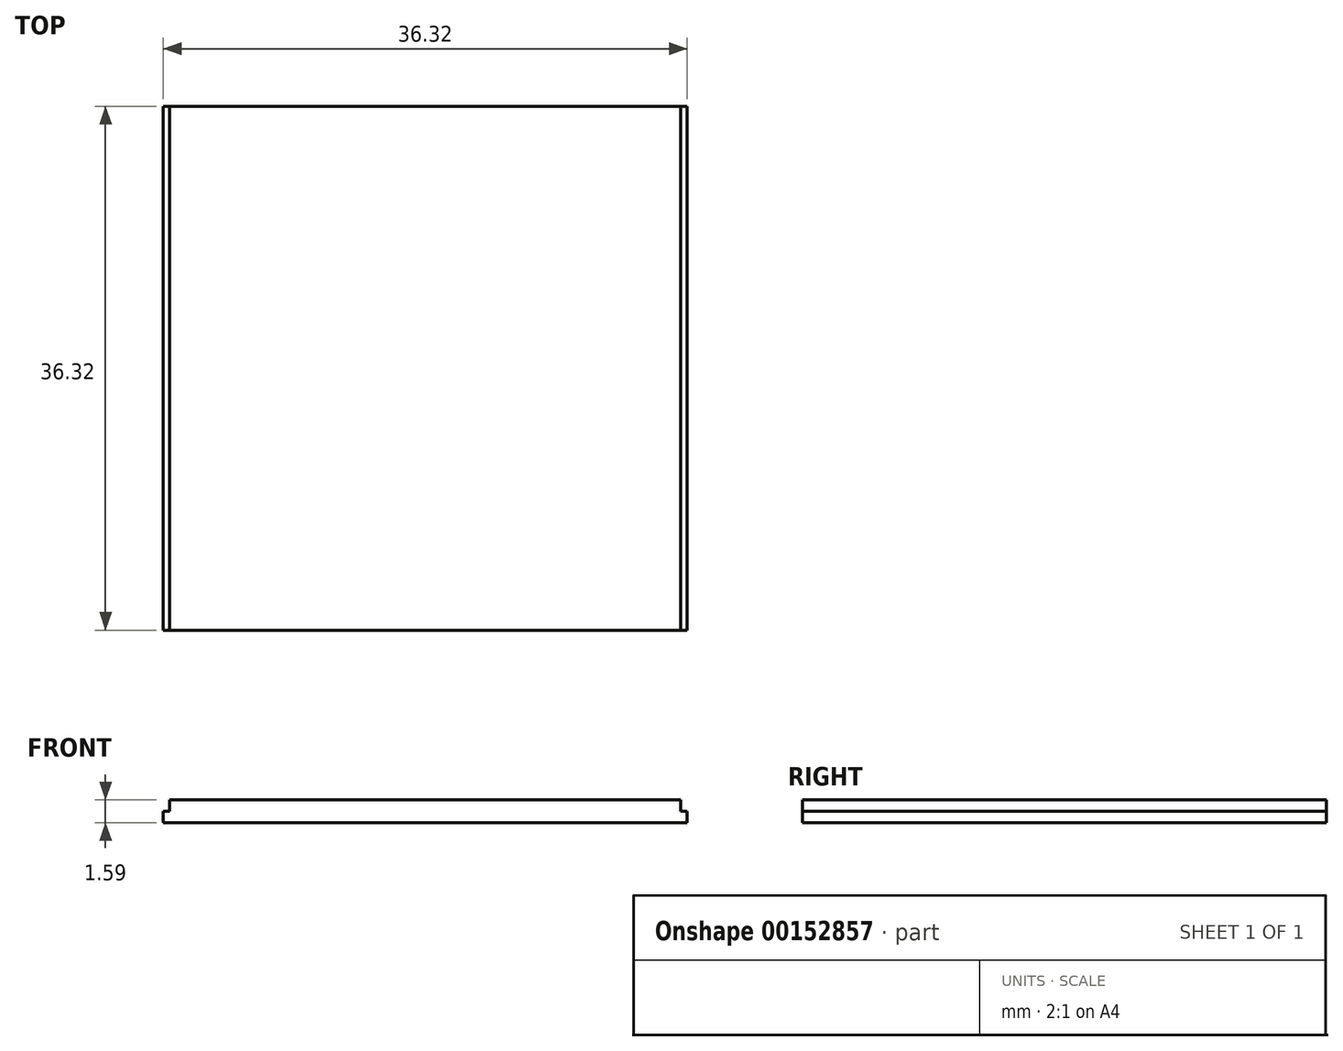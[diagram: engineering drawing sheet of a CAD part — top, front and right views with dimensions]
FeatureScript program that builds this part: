
annotation { "Feature Type Name" : "Feature", "Feature Type Description" : "" }
export const myFeature = defineFeature(function(context is Context, id is Id, definition is map)
    precondition{}
    {
        {
            var Q0;
            Q0=qCreatedBy(makeId("Top.planeOp"),FACE);
            var sketch = newSketch(context, id + "F0", { "sketchPlane" : qUnion([Q0])});
            skLineSegment(sketch, "E0.bottom", {"start": v(0, 0) * mm, "end": v(36.32, 0) * mm});
            skLineSegment(sketch, "E0.top", {"start": v(0, -36.32) * mm, "end": v(36.32, -36.32) * mm});
            skLineSegment(sketch, "E0.left", {"start": v(0, 0) * mm, "end": v(0, -36.32) * mm});
            skLineSegment(sketch, "E0.right", {"start": v(36.32, 0) * mm, "end": v(36.32, -36.32) * mm});
            skSolve(sketch);
        }
        {
            var Q0;
            Q0 = qSketchRegion(id + "F0", true);
            extrude(context, id + "F1", {"entities" : qUnion([Q0]), "depth" : 0.8 * mm});
        }
        {
            var Q0;
            Q0=makeQuery(id+"F1.opExtrude","CAP_FACE",FACE,{"disambiguationData":[OSD([sQuery(id+"F0.wireOp",EDGE,"E0.bottom"),sQuery(id+"F0.wireOp",EDGE,"E0.top"),sQuery(id+"F0.wireOp",EDGE,"E0.left"),sQuery(id+"F0.wireOp",EDGE,"E0.right")])],"isStart":false});
            var sketch = newSketch(context, id + "F2", { "sketchPlane" : qUnion([Q0])});
            skPoint(sketch, "E1", {"position": v(18.16, -36.32) * mm});
            skLineSegment(sketch, "E2.bottom", {"start": v(0.44, -36.32) * mm, "end": v(35.88, -36.32) * mm});
            skLineSegment(sketch, "E2.top", {"start": v(0.44, 0) * mm, "end": v(35.88, 0) * mm});
            skLineSegment(sketch, "E2.left", {"start": v(0.44, -36.32) * mm, "end": v(0.44, 0) * mm});
            skLineSegment(sketch, "E2.right", {"start": v(35.88, -36.32) * mm, "end": v(35.88, 0) * mm});
            skSolve(sketch);
        }
        {
            var Q0;
            Q0 = qSketchRegion(id + "F2", true);
            extrude(context, id + "F3", {"entities" : qUnion([Q0]), "operationType" : NewBodyOperationType.ADD, "depth" : 0.8 * mm});
        }
    });
